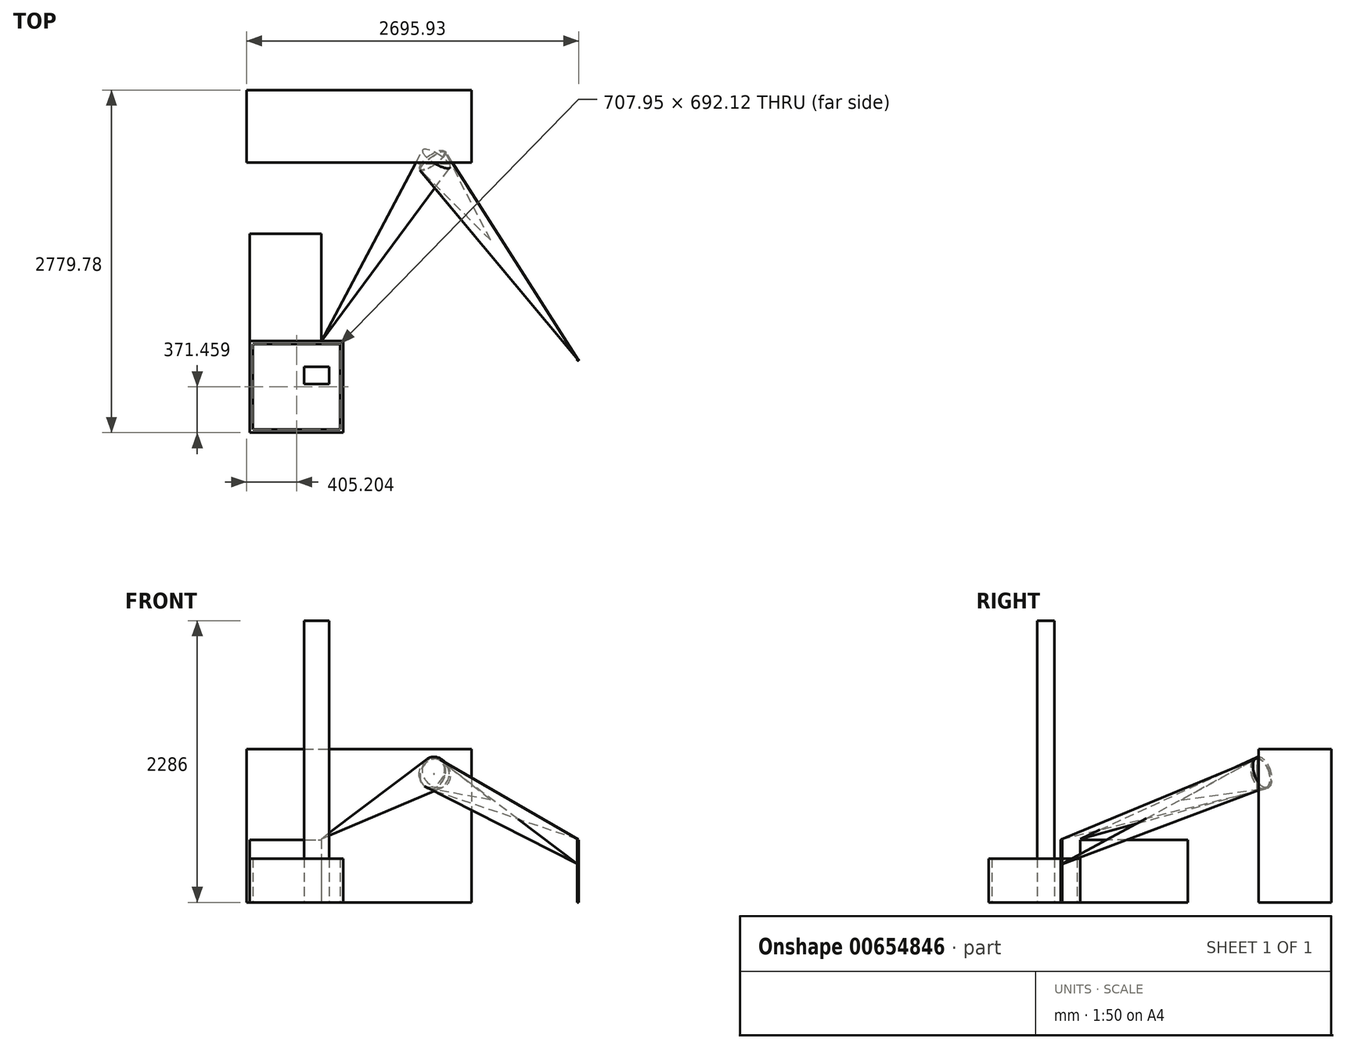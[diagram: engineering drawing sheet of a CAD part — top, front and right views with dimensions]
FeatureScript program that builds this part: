
annotation { "Feature Type Name" : "Feature", "Feature Type Description" : "" }
export const myFeature = defineFeature(function(context is Context, id is Id, definition is map)
    precondition{}
    {
        {
            var Q0;
            Q0=qCreatedBy(makeId("Top.planeOp"),FACE);
            var sketch = newSketch(context, id + "F0", { "sketchPlane" : qUnion([Q0])});
            skLineSegment(sketch, "E0.bottom", {"start": v(-1117.06, 1219.02) * mm, "end": v(708.92, 1219.02) * mm});
            skLineSegment(sketch, "E0.top", {"start": v(-1117.06, 629.96) * mm, "end": v(708.92, 629.96) * mm});
            skLineSegment(sketch, "E0.left", {"start": v(-1117.06, 1219.02) * mm, "end": v(-1117.06, 629.96) * mm});
            skLineSegment(sketch, "E0.right", {"start": v(708.92, 1219.02) * mm, "end": v(708.92, 629.96) * mm});
            skLineSegment(sketch, "E1.bottom", {"start": v(-1091.23, 53.93) * mm, "end": v(-510.28, 53.93) * mm});
            skLineSegment(sketch, "E1.top", {"start": v(-1091.23, -817.84) * mm, "end": v(-510.28, -817.84) * mm});
            skLineSegment(sketch, "E1.left", {"start": v(-1091.23, 53.93) * mm, "end": v(-1091.23, -817.84) * mm});
            skLineSegment(sketch, "E1.right", {"start": v(-510.28, 53.93) * mm, "end": v(-510.28, -817.84) * mm});
            skCircle(sketch, "E2", {"center": v(1572.52, -970.24) * mm, "radius": 6.35 * mm});
            skLineSegment(sketch, "E3.bottom", {"start": v(-1091.23, -817.84) * mm, "end": v(-332.48, -817.84) * mm});
            skLineSegment(sketch, "E3.top", {"start": v(-1091.23, -1560.76) * mm, "end": v(-332.48, -1560.76) * mm});
            skLineSegment(sketch, "E3.left", {"start": v(-1091.23, -817.84) * mm, "end": v(-1091.23, -1560.76) * mm});
            skLineSegment(sketch, "E3.right", {"start": v(-332.48, -817.84) * mm, "end": v(-332.48, -1560.76) * mm});
            skLineSegment(sketch, "E4.0", {"start": v(-1065.83, -843.24) * mm, "end": v(-357.88, -843.24) * mm});
            skLineSegment(sketch, "E4.1", {"start": v(-1065.83, -843.24) * mm, "end": v(-1065.83, -1535.36) * mm});
            skLineSegment(sketch, "E4.2", {"start": v(-1065.83, -1535.36) * mm, "end": v(-357.88, -1535.36) * mm});
            skLineSegment(sketch, "E4.3", {"start": v(-357.88, -843.24) * mm, "end": v(-357.88, -1535.36) * mm});
            skLineSegment(sketch, "E5.bottom", {"start": v(-649.36, -1027.67) * mm, "end": v(-446.93, -1027.67) * mm});
            skLineSegment(sketch, "E5.top", {"start": v(-649.36, -1167.02) * mm, "end": v(-446.93, -1167.02) * mm});
            skLineSegment(sketch, "E5.left", {"start": v(-649.36, -1027.67) * mm, "end": v(-649.36, -1167.02) * mm});
            skLineSegment(sketch, "E5.right", {"start": v(-446.93, -1027.67) * mm, "end": v(-446.93, -1167.02) * mm});
            skSolve(sketch);
        }
        {
            var Q0;
            Q0=makeQuery(id+"F0.imprint","IMPRINT",FACE,{"disambiguationData":[TD([[makeQuery(id+"F0.imprint","IMPRINT",EDGE,{"derivedFrom":sQuery(id+"F0.wireOp",EDGE,"E1.bottom")}),-1.0]])]});
            extrude(context, id + "F1", {"entities" : qUnion([Q0]), "depth" : 508 * mm, "offsetDistance" : 25.4 * mm});
        }
        {
            var Q0;
            Q0=makeQuery(id+"F0.imprint","IMPRINT",FACE,{"disambiguationData":[TD([[makeQuery(id+"F0.imprint","IMPRINT",EDGE,{"derivedFrom":sQuery(id+"F0.wireOp",EDGE,"E0.bottom")}),-1.0]])]});
            extrude(context, id + "F2", {"entities" : qUnion([Q0]), "depth" : 1244.6 * mm, "offsetDistance" : 25.4 * mm});
        }
        {
            var Q0;
            Q0=makeQuery(id+"F0.imprint","IMPRINT",FACE,{"disambiguationData":[TD([[makeQuery(id+"F0.imprint","IMPRINT",EDGE,{"derivedFrom":sQuery(id+"F0.wireOp",EDGE,"E2")}),1.0]])]});
            extrude(context, id + "F3", {"entities" : qUnion([Q0]), "depth" : 508 * mm, "offsetDistance" : 25.4 * mm});
        }
        {
            var Q0;
            Q0=makeQuery(id+"F2.opExtrude","SWEPT_FACE",FACE,{"disambiguationData":[OSD([sQuery(id+"F0.wireOp",EDGE,"E0.top")])]});
            var sketch = newSketch(context, id + "F4", { "sketchPlane" : qUnion([Q0])});
            skCircle(sketch, "E6", {"center": v(404.12, 1041.4) * mm, "radius": 124.2 * mm});
            skCircle(sketch, "E7", {"center": v(404.12, 1041.4) * mm, "radius": 1.88 * mm});
            skSolve(sketch);
        }
        {
            var Q0;
            Q0=makeQuery(id+"F4.imprint","IMPRINT",FACE,{"disambiguationData":[TD([[makeQuery(id+"F4.imprint","IMPRINT",EDGE,{"derivedFrom":sQuery(id+"F4.wireOp",EDGE,"E6")}),1.0]])]});
            extrude(context, id + "F5", {"entities" : qUnion([Q0]), "operationType" : NewBodyOperationType.ADD, "depth" : 12.7 * mm, "offsetDistance" : 25.4 * mm});
        }
        {
            var Q0;
            Q0=makeQuery(id+"F3.opExtrude","CAP_FACE",FACE,{"disambiguationData":[OSD([sQuery(id+"F0.wireOp",EDGE,"E2")])],"isStart":false});
            var sketch = newSketch(context, id + "F6", { "sketchPlane" : qUnion([Q0])});
            skCircle(sketch, "E8", {"center": v(1572.52, -970.24) * mm, "radius": 0.64 * mm});
            skSolve(sketch);
        }
        {
            var Q0;
            Q0=sQuery(id+"F4.wireOp",VERTEX,"E6.center");
            var Q1;
            Q1=sQuery(id+"F0.wireOp",VERTEX,"E2.center");
            var Q2;
            Q2=sQuery(id+"F6.wireOp",VERTEX,"E8.center");
            cPlane(context, id + "F7", {"entities" : qUnion([Q0, Q1, Q2]), "cplaneType" : CPlaneType.THREE_POINT, "offset" : 25.4 * mm, "width" : 152.4 * mm, "height" : 152.4 * mm});
        }
        {
            var Q0;
            Q0=qCreatedBy(id+"F7.planeOp",FACE);
            var sketch = newSketch(context, id + "F8", { "sketchPlane" : qUnion([Q0])});
            skLineSegment(sketch, "E9", {"start": v(263.46, 1166.8) * mm, "end": v(-1712.42, 307.85) * mm});
            skLineSegment(sketch, "E10", {"start": v(-1712.42, 307.85) * mm, "end": v(272.24, 1039.95) * mm});
            skLineSegment(sketch, "E11", {"start": v(272.24, 1039.95) * mm, "end": v(263.46, 1166.8) * mm});
            skLineSegment(sketch, "E12", {"start": v(-1714.63, 510.24) * mm, "end": v(263.46, 1036.7) * mm});
            skLineSegment(sketch, "E13", {"start": v(263.46, 1036.7) * mm, "end": v(254.45, 1166.8) * mm});
            skLineSegment(sketch, "E14", {"start": v(254.45, 1166.8) * mm, "end": v(-1714.63, 510.24) * mm});
            skSolve(sketch);
        }
        {
            var Q0;
            Q0=makeQuery(id+"F8.imprint","IMPRINT",FACE,{"disambiguationData":[TD([[makeQuery(id+"F8.imprint","IMPRINT",EDGE,{"derivedFrom":sQuery(id+"F8.wireOp",EDGE,"E9")}),1.0]])]});
            var Q1;
            Q1=sQuery(id+"F8.wireOp",EDGE,"E10");
            revolve(context, id + "F9", {"entities" : qUnion([Q0]), "axis" : qUnion([Q1]), "revolveType" : RevolveType.FULL});
        }
        {
            var Q0;
            Q0=makeQuery(id+"F0.imprint","IMPRINT",FACE,{"disambiguationData":[TD([[makeQuery(id+"F0.imprint","IMPRINT",EDGE,{"derivedFrom":sQuery(id+"F0.wireOp",EDGE,"E3.top")}),1.0]])]});
            extrude(context, id + "F10", {"entities" : qUnion([Q0]), "operationType" : NewBodyOperationType.ADD, "depth" : 355.6 * mm, "offsetDistance" : 25.4 * mm});
        }
        {
            var Q0;
            Q0=makeQuery(id+"F0.imprint","IMPRINT",FACE,{"disambiguationData":[TD([[makeQuery(id+"F0.imprint","IMPRINT",EDGE,{"derivedFrom":sQuery(id+"F0.wireOp",EDGE,"E5.bottom")}),-1.0]])]});
            extrude(context, id + "F11", {"entities" : qUnion([Q0]), "depth" : 2286 * mm, "offsetDistance" : 25.4 * mm});
        }
        {
            var Q0;
            Q0=makeQuery(id+"F1.opExtrude","CAP_VERTEX",VERTEX,{"disambiguationData":[OSD([sQuery(id+"F0.wireOp",EDGE,"E1.right"),sQuery(id+"F0.wireOp",EDGE,"E3.bottom")])],"isStart":false});
            var Q1;
            Q1=sQuery(id+"F0.wireOp",VERTEX,"E1.top.end");
            var Q2;
            Q2=sQuery(id+"F4.wireOp",VERTEX,"E7.center");
            cPlane(context, id + "F12", {"entities" : qUnion([Q0, Q1, Q2]), "cplaneType" : CPlaneType.THREE_POINT, "offset" : 25.4 * mm, "width" : 152.4 * mm, "height" : 152.4 * mm});
        }
        {
            var Q0;
            Q0=qCreatedBy(id+"F12.planeOp",FACE);
            var sketch = newSketch(context, id + "F13", { "sketchPlane" : qUnion([Q0])});
            skLineSegment(sketch, "E15", {"start": v(966.46, 514.14) * mm, "end": v(-746.5, 1180.19) * mm});
            skLineSegment(sketch, "E16", {"start": v(-746.5, 1180.19) * mm, "end": v(-748.73, 1042.75) * mm});
            skLineSegment(sketch, "E17", {"start": v(-748.73, 1042.75) * mm, "end": v(966.46, 514.14) * mm});
            skSolve(sketch);
        }
        {
            var Q0;
            Q0=makeQuery(id+"F13.imprint","IMPRINT",FACE,{"disambiguationData":[TD([[makeQuery(id+"F13.imprint","IMPRINT",EDGE,{"derivedFrom":sQuery(id+"F13.wireOp",EDGE,"E15")}),1.0]])]});
            var Q1;
            Q1=sQuery(id+"F13.wireOp",EDGE,"E17");
            revolve(context, id + "F14", {"entities" : qUnion([Q0]), "axis" : qUnion([Q1]), "revolveType" : RevolveType.FULL});
        }
        {
            var Q0;
            {var subQ5=sQuery(id+"F8.wireOp",EDGE,"E14");Q0=makeQuery(id+"F8.imprint","IMPRINT",FACE,{"disambiguationData":[TD([[makeQuery(id+"F8.imprint","IMPRINT",EDGE,{"derivedFrom":subQ5}),1.0]])]});}
            var Q1;
            Q1=sQuery(id+"F8.wireOp",EDGE,"E12");
            revolve(context, id + "F15", {"entities" : qUnion([Q0]), "axis" : qUnion([Q1]), "revolveType" : RevolveType.FULL});
        }
    });
